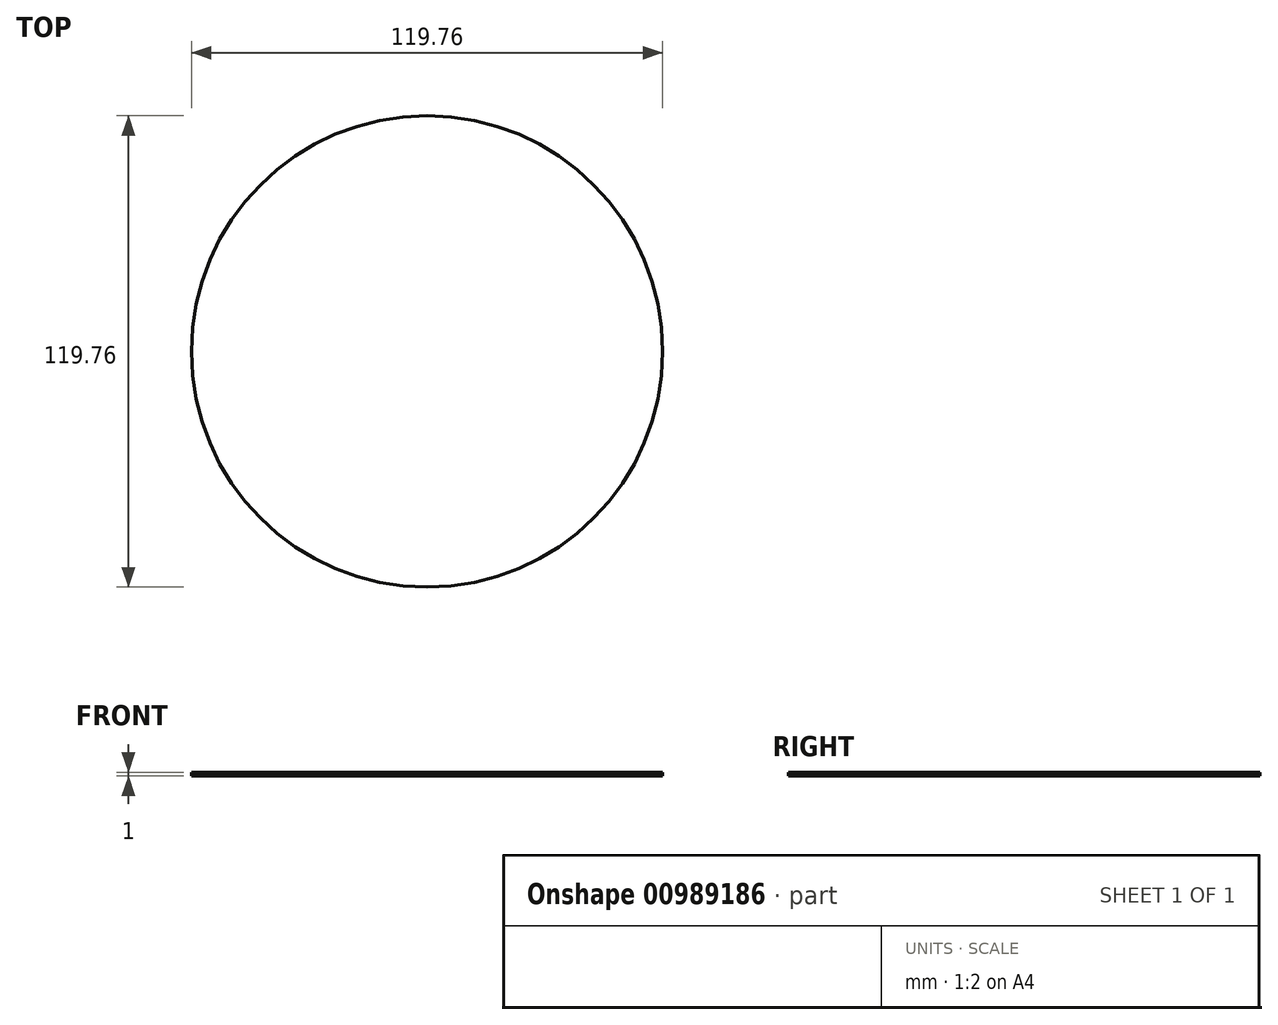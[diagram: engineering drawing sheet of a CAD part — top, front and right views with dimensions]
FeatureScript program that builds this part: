
annotation { "Feature Type Name" : "Feature", "Feature Type Description" : "" }
export const myFeature = defineFeature(function(context is Context, id is Id, definition is map)
    precondition{}
    {
        {
            var Q0;
            Q0=qCreatedBy(makeId("Top.planeOp"),FACE);
            var sketch = newSketch(context, id + "F0", { "sketchPlane" : qUnion([Q0])});
            skCircle(sketch, "E0", {"center": v(0, 0) * mm, "radius": 59.88 * mm});
            skSolve(sketch);
        }
        {
            var Q0;
            Q0=makeQuery(id+"F0.imprint","IMPRINT",FACE,{"disambiguationData":[TD([[makeQuery(id+"F0.imprint","IMPRINT",EDGE,{"derivedFrom":sQuery(id+"F0.wireOp",EDGE,"E0")}),1.0]])]});
            extrude(context, id + "F1", {"entities" : qUnion([Q0]), "depth" : 1 * mm, "offsetDistance" : 25.4 * mm});
        }
        {
            var Q0;
            Q0=makeQuery(id+"F1.opExtrude","CAP_FACE",FACE,{"disambiguationData":[OSD([sQuery(id+"F0.wireOp",EDGE,"E0")])],"isStart":false});
            var sketch = newSketch(context, id + "F2", { "sketchPlane" : qUnion([Q0])});
            skFitSpline(sketch, "E1", {"points": [v(-48.5, 0) * mm, v(-49.78, -18.98) * mm, v(43.37, 26.78) * mm, v(-42.13, -11.14) * mm, v(-48.5, 0) * mm]});
            skSolve(sketch);
        }
        {
            var Q0;
            Q0=sQuery(id+"F2.wireOp",EDGE,"E1");
            extrude(context, id + "F3", {"bodyType" : ToolBodyType.SURFACE, "surfaceEntities" : qUnion([Q0]), "depth" : 2 * mm, "offsetDistance" : 25.4 * mm});
        }
    });
